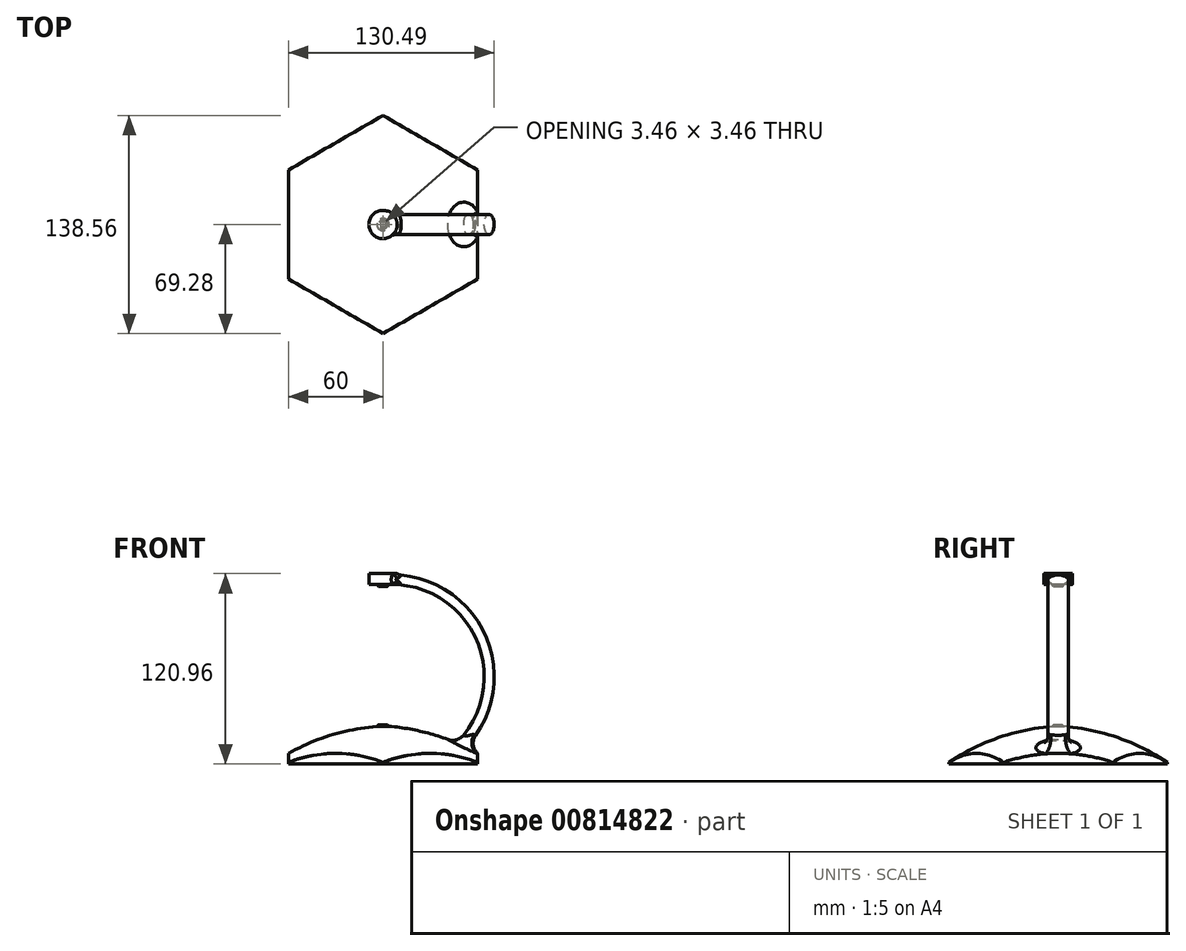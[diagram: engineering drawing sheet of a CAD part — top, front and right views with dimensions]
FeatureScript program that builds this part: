
annotation { "Feature Type Name" : "Feature", "Feature Type Description" : "" }
export const myFeature = defineFeature(function(context is Context, id is Id, definition is map)
    precondition{}
    {
        {
            var Q0;
            Q0=qCreatedBy(makeId("Top.planeOp"),FACE);
            var sketch = newSketch(context, id + "F0", { "sketchPlane" : qUnion([Q0])});
            skCircle(sketch, "E0.cCircle", {"center": v(0, 0) * mm, "radius": 60 * mm, "construction": true});
            skLineSegment(sketch, "E0.0", {"start": v(60, 34.64) * mm, "end": v(60, -34.64) * mm});
            skLineSegment(sketch, "E0.1", {"start": v(60, -34.64) * mm, "end": v(0, -69.28) * mm});
            skLineSegment(sketch, "E0.2", {"start": v(0, -69.28) * mm, "end": v(-60, -34.64) * mm});
            skLineSegment(sketch, "E0.3", {"start": v(-60, -34.64) * mm, "end": v(-60, 34.64) * mm});
            skLineSegment(sketch, "E0.4", {"start": v(-60, 34.64) * mm, "end": v(0, 69.28) * mm});
            skLineSegment(sketch, "E0.5", {"start": v(0, 69.28) * mm, "end": v(60, 34.64) * mm});
            skPoint(sketch, "E0.0.midPoint", {"position": v(60, 0) * mm});
            skSolve(sketch);
        }
        {
            var Q0;
            Q0 = qSketchRegion(id + "F0", true);
            extrude(context, id + "F1", {"entities" : qUnion([Q0]), "depth" : 37.8 * mm, "offsetDistance" : 25 * mm});
        }
        {
            var Q0;
            Q0=qCreatedBy(makeId("Front.planeOp"),FACE);
            var sketch = newSketch(context, id + "F2", { "sketchPlane" : qUnion([Q0])});
            skLineSegment(sketch, "E1", {"start": v(0, 30) * mm, "end": v(1.73, 31) * mm});
            skLineSegment(sketch, "E2", {"start": v(1.73, 31) * mm, "end": v(2.86, 31) * mm});
            skLineSegment(sketch, "E3", {"start": v(2.86, 31) * mm, "end": v(3.86, 30) * mm});
            skArc(sketch, "E4", {"start": v(92.95, -12.94) * mm, "mid": v(52.4, 16.84) * mm, "end": v(3.86, 30) * mm});
            skLineSegment(sketch, "E5", {"start": v(92.95, -12.94) * mm, "end": v(92.95, 44.68) * mm});
            skLineSegment(sketch, "E6", {"start": v(92.95, 44.68) * mm, "end": v(0, 44.68) * mm});
            skLineSegment(sketch, "E7", {"start": v(0, 44.68) * mm, "end": v(0, 30) * mm});
            skSolve(sketch);
        }
        {
            var Q0;
            Q0 = qSketchRegion(id + "F2", true);
            var Q1;
            Q1=sQuery(id+"F2.wireOp",EDGE,"E7");
            revolve(context, id + "F3", {"operationType" : NewBodyOperationType.REMOVE, "surfaceOperationType" : NewSurfaceOperationType.NEW, "entities" : qUnion([Q0]), "axis" : qUnion([Q1]), "revolveType" : RevolveType.FULL, "oppositeDirection" : true});
        }
        {
            var Q0;
            Q0=qCreatedBy(makeId("Front.planeOp"),FACE);
            var sketch = newSketch(context, id + "F4", { "sketchPlane" : qUnion([Q0])});
            skLineSegment(sketch, "E8", {"start": v(0, 120) * mm, "end": v(1.73, 119) * mm});
            skLineSegment(sketch, "E9", {"start": v(1.73, 119) * mm, "end": v(2.9, 119) * mm});
            skLineSegment(sketch, "E10", {"start": v(2.9, 119) * mm, "end": v(3.9, 120) * mm});
            skLineSegment(sketch, "E11", {"start": v(3.9, 120) * mm, "end": v(9, 120) * mm});
            skLineSegment(sketch, "E12", {"start": v(9, 120) * mm, "end": v(9, 127) * mm});
            skLineSegment(sketch, "E13", {"start": v(9, 127) * mm, "end": v(0, 127) * mm});
            skLineSegment(sketch, "E14", {"start": v(0, 127) * mm, "end": v(0, 120) * mm});
            skSolve(sketch);
        }
        {
            var Q0;
            Q0 = qSketchRegion(id + "F4", true);
            var Q1;
            Q1=sQuery(id+"F4.wireOp",EDGE,"E14");
            revolve(context, id + "F5", {"surfaceOperationType" : NewSurfaceOperationType.NEW, "entities" : qUnion([Q0]), "axis" : qUnion([Q1]), "revolveType" : RevolveType.FULL});
        }
        {
            var Q0;
            Q0=qCreatedBy(makeId("Front.planeOp"),FACE);
            var sketch = newSketch(context, id + "F6", { "sketchPlane" : qUnion([Q0])});
            skArc(sketch, "E15", {"start": v(0, 0) * mm, "mid": v(67.38, 61.5) * mm, "end": v(0, 123.02) * mm});
            skSolve(sketch);
        }
        {
            var Q0;
            Q0=qCreatedBy(makeId("Right.planeOp"),FACE);
            var sketch = newSketch(context, id + "F7", { "sketchPlane" : qUnion([Q0])});
            skEllipse(sketch, "E16", {"center": v(0, 0) * mm, "majorRadius": 6.4 * mm, "minorRadius": 3.13 * mm, "majorAxis": v(1, 0)});
            skSolve(sketch);
        }
        {
            var Q0;
            Q0 = qSketchRegion(id + "F7", true);
            var Q1;
            Q1=sQuery(id+"F6.wireOp",EDGE,"E15");
            sweep(context, id + "F8", {"profiles" : qUnion([Q0]), "path" : qUnion([Q1])});
        }
        {
            var Q0;
            Q0=makeQuery(id+"F1.opExtrude","SWEPT_BODY",BODY,{"disambiguationData":[OSD([sQuery(id+"F0.wireOp",EDGE,"E0.0"),sQuery(id+"F0.wireOp",EDGE,"E0.1"),sQuery(id+"F0.wireOp",EDGE,"E0.2"),sQuery(id+"F0.wireOp",EDGE,"E0.3"),sQuery(id+"F0.wireOp",EDGE,"E0.4"),sQuery(id+"F0.wireOp",EDGE,"E0.5")])]});
            var Q1;
            Q1=makeQuery(id+"F5.opRevolve","SWEPT_BODY",BODY,{"disambiguationData":[OSD([sQuery(id+"F4.wireOp",EDGE,"E8"),sQuery(id+"F4.wireOp",EDGE,"E9"),sQuery(id+"F4.wireOp",EDGE,"E10"),sQuery(id+"F4.wireOp",EDGE,"E11"),sQuery(id+"F4.wireOp",EDGE,"E12"),sQuery(id+"F4.wireOp",EDGE,"E13"),sQuery(id+"F4.wireOp",EDGE,"E14")])]});
            var Q2;
            Q2=makeQuery(id+"F8.opSweep","SWEPT_BODY",BODY,{"disambiguationData":[OSD([sQuery(id+"F6.wireOp",EDGE,"E15"),sQuery(id+"F7.wireOp",EDGE,"E16")])]});
            booleanBodies(context, id + "F9", {"operationType" : BooleanOperationType.UNION, "tools" : qUnion([Q0, Q1, Q2])});
        }
        {
            var Q0;
            Q0=makeQuery(id+"F9.opBoolean","INTERSECT",EDGE,{"derivedFrom":[makeQuery(id+"F3.boolean.opBoolean","COPY",FACE,{"derivedFrom":makeQuery(id+"F3.opRevolve","SWEPT_FACE",FACE,{"disambiguationData":[OSD([sQuery(id+"F2.wireOp",EDGE,"E4")])]})}),makeQuery(id+"F8.opSweep","SWEPT_FACE",FACE,{"disambiguationData":[OSD([sQuery(id+"F6.wireOp",EDGE,"E15"),sQuery(id+"F7.wireOp",EDGE,"E16")])]})]});
            fillet(context, id + "F10", {"entities" : qUnion([Q0]), "radius" : 8.75 * mm, "tangentPropagation" : true, "allowEdgeOverflow" : false});
        }
        {
            var Q0;
            Q0=makeQuery(id+"F9.opBoolean","INTERSECT",EDGE,{"derivedFrom":[makeQuery(id+"F5.opRevolve","SWEPT_FACE",FACE,{"disambiguationData":[OSD([sQuery(id+"F4.wireOp",EDGE,"E12")])]}),makeQuery(id+"F8.opSweep","SWEPT_FACE",FACE,{"disambiguationData":[OSD([sQuery(id+"F6.wireOp",EDGE,"E15"),sQuery(id+"F7.wireOp",EDGE,"E16")])]})]});
            fillet(context, id + "F11", {"entities" : qUnion([Q0]), "radius" : 5 * mm, "tangentPropagation" : true, "allowEdgeOverflow" : false});
        }
        {
            var Q0;
            Q0=qCreatedBy(makeId("Front.planeOp"),FACE);
            var sketch = newSketch(context, id + "F12", { "sketchPlane" : qUnion([Q0])});
            skLineSegment(sketch, "E17.bottom", {"start": v(-72.98, -24.67) * mm, "end": v(84.85, -24.67) * mm});
            skLineSegment(sketch, "E17.top", {"start": v(-72.98, 6.04) * mm, "end": v(84.85, 6.04) * mm});
            skLineSegment(sketch, "E17.left", {"start": v(-72.98, -24.67) * mm, "end": v(-72.98, 6.04) * mm});
            skLineSegment(sketch, "E17.right", {"start": v(84.85, -24.67) * mm, "end": v(84.85, 6.04) * mm});
            skSolve(sketch);
        }
        {
            var Q0;
            Q0=makeQuery(id+"F12.imprint","IMPRINT",FACE,{"disambiguationData":[TD([[makeQuery(id+"F12.imprint","IMPRINT",EDGE,{"derivedFrom":sQuery(id+"F12.wireOp",EDGE,"E17.bottom")}),1.0]])]});
            extrude(context, id + "F13", {"entities" : qUnion([Q0]), "operationType" : NewBodyOperationType.REMOVE, "endBound" : BoundingType.THROUGH_ALL, "oppositeDirection" : true, "depth" : 25 * mm, "offsetDistance" : 25 * mm, "hasSecondDirection" : true, "secondDirectionBound" : SecondDirectionBoundingType.THROUGH_ALL, "secondDirectionOppositeDirection" : false, "secondDirectionDepth" : 25 * mm});
        }
    });
